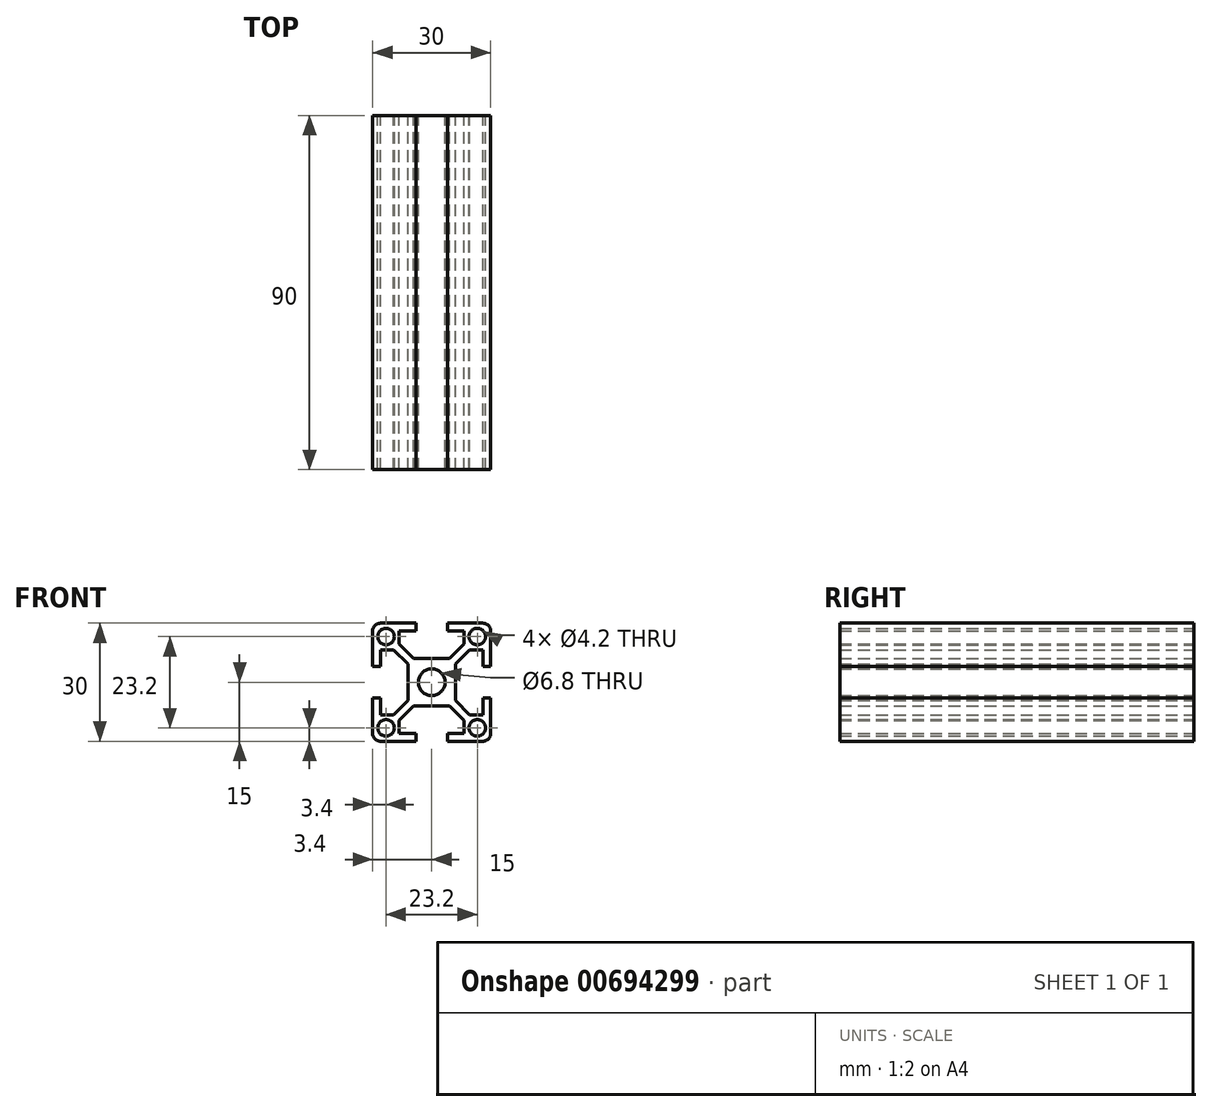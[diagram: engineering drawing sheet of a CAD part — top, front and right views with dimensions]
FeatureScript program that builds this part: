
annotation { "Feature Type Name" : "Feature", "Feature Type Description" : "" }
export const myFeature = defineFeature(function(context is Context, id is Id, definition is map)
    precondition{}
    {
        {
            var Q0;
            Q0=qCreatedBy(makeId("Front.planeOp"),FACE);
            var sketch = newSketch(context, id + "F0", { "sketchPlane" : qUnion([Q0])});
            skLineSegment(sketch, "E0", {"start": v(0, 6) * mm, "end": v(-4.59, 6) * mm});
            skLineSegment(sketch, "E1", {"start": v(-4.59, 6) * mm, "end": v(-8.25, 9.66) * mm});
            skLineSegment(sketch, "E2", {"start": v(-8.25, 9.66) * mm, "end": v(-8.25, 13) * mm});
            skLineSegment(sketch, "E3", {"start": v(-8.25, 13) * mm, "end": v(-4, 13) * mm});
            skLineSegment(sketch, "E4", {"start": v(-4, 13) * mm, "end": v(-4, 15) * mm});
            skLineSegment(sketch, "E5", {"start": v(-4, 15) * mm, "end": v(-13, 15) * mm});
            skLineSegment(sketch, "E6", {"start": v(-15, 13) * mm, "end": v(-15, 4) * mm});
            skLineSegment(sketch, "E7", {"start": v(-15, 4) * mm, "end": v(-13, 4) * mm});
            skLineSegment(sketch, "E8", {"start": v(-13, 4) * mm, "end": v(-13, 8.25) * mm});
            skLineSegment(sketch, "E9", {"start": v(-13, 8.25) * mm, "end": v(-9.66, 8.25) * mm});
            skLineSegment(sketch, "E10", {"start": v(-9.66, 8.25) * mm, "end": v(-6, 4.59) * mm});
            skLineSegment(sketch, "E11", {"start": v(-6, 4.59) * mm, "end": v(-6, 0) * mm});
            skLineSegment(sketch, "E12", {"start": v(-6, 0) * mm, "end": v(0, 0) * mm, "construction": true});
            skLineSegment(sketch, "E13", {"start": v(0, 0) * mm, "end": v(0, 6) * mm, "construction": true});
            skArc(sketch, "E14", {"start": v(0, 3.4) * mm, "mid": v(-2.4, 2.4) * mm, "end": v(-3.4, 0) * mm});
            skCircle(sketch, "E15", {"center": v(-11.6, 11.6) * mm, "radius": 2.1 * mm});
            skLineSegment(sketch, "E16", {"start": v(0, 0) * mm, "end": v(-7.38, 7.38) * mm, "construction": true});
            skLineSegment(sketch, "E17.1.0", {"start": v(-8.25, -13) * mm, "end": v(-8.25, -9.66) * mm});
            skLineSegment(sketch, "E17.1.1", {"start": v(-4, -15) * mm, "end": v(-4, -13) * mm});
            skLineSegment(sketch, "E17.1.2", {"start": v(-4, -13) * mm, "end": v(-8.25, -13) * mm});
            skLineSegment(sketch, "E17.1.3", {"start": v(-15, -4) * mm, "end": v(-15, -13) * mm});
            skLineSegment(sketch, "E17.1.4", {"start": v(-8.25, -9.66) * mm, "end": v(-4.59, -6) * mm});
            skLineSegment(sketch, "E17.1.5", {"start": v(-13, -15) * mm, "end": v(-4, -15) * mm});
            skLineSegment(sketch, "E17.1.6", {"start": v(-4.59, -6) * mm, "end": v(0, -6) * mm});
            skLineSegment(sketch, "E17.1.7", {"start": v(0, -6) * mm, "end": v(0, 0) * mm, "construction": true});
            skLineSegment(sketch, "E17.1.8", {"start": v(0, 0) * mm, "end": v(-6, 0) * mm, "construction": true});
            skLineSegment(sketch, "E17.1.9", {"start": v(-13, -4) * mm, "end": v(-15, -4) * mm});
            skLineSegment(sketch, "E17.1.10", {"start": v(-13, -8.25) * mm, "end": v(-13, -4) * mm});
            skArc(sketch, "E17.1.11", {"start": v(-3.4, 0) * mm, "mid": v(-2.4, -2.4) * mm, "end": v(0, -3.4) * mm});
            skLineSegment(sketch, "E17.1.12", {"start": v(-9.66, -8.25) * mm, "end": v(-13, -8.25) * mm});
            skLineSegment(sketch, "E17.1.13", {"start": v(0, 0) * mm, "end": v(-7.38, -7.38) * mm, "construction": true});
            skLineSegment(sketch, "E17.1.14", {"start": v(-6, -4.59) * mm, "end": v(-9.66, -8.25) * mm});
            skCircle(sketch, "E17.1.15", {"center": v(-11.6, -11.6) * mm, "radius": 2.1 * mm});
            skLineSegment(sketch, "E17.1.16", {"start": v(-6, 0) * mm, "end": v(-6, -4.59) * mm});
            skLineSegment(sketch, "E17.2.0", {"start": v(13, -8.25) * mm, "end": v(9.66, -8.25) * mm});
            skLineSegment(sketch, "E17.2.1", {"start": v(15, -4) * mm, "end": v(13, -4) * mm});
            skLineSegment(sketch, "E17.2.2", {"start": v(13, -4) * mm, "end": v(13, -8.25) * mm});
            skLineSegment(sketch, "E17.2.3", {"start": v(4, -15) * mm, "end": v(13, -15) * mm});
            skLineSegment(sketch, "E17.2.4", {"start": v(9.66, -8.25) * mm, "end": v(6, -4.59) * mm});
            skLineSegment(sketch, "E17.2.5", {"start": v(15, -13) * mm, "end": v(15, -4) * mm});
            skLineSegment(sketch, "E17.2.6", {"start": v(6, -4.59) * mm, "end": v(6, 0) * mm});
            skLineSegment(sketch, "E17.2.7", {"start": v(6, 0) * mm, "end": v(0, 0) * mm, "construction": true});
            skLineSegment(sketch, "E17.2.8", {"start": v(0, 0) * mm, "end": v(0, -6) * mm, "construction": true});
            skLineSegment(sketch, "E17.2.9", {"start": v(4, -13) * mm, "end": v(4, -15) * mm});
            skLineSegment(sketch, "E17.2.10", {"start": v(8.25, -13) * mm, "end": v(4, -13) * mm});
            skArc(sketch, "E17.2.11", {"start": v(0, -3.4) * mm, "mid": v(2.4, -2.4) * mm, "end": v(3.4, 0) * mm});
            skLineSegment(sketch, "E17.2.12", {"start": v(8.25, -9.66) * mm, "end": v(8.25, -13) * mm});
            skLineSegment(sketch, "E17.2.13", {"start": v(0, 0) * mm, "end": v(7.38, -7.38) * mm, "construction": true});
            skLineSegment(sketch, "E17.2.14", {"start": v(4.59, -6) * mm, "end": v(8.25, -9.66) * mm});
            skCircle(sketch, "E17.2.15", {"center": v(11.6, -11.6) * mm, "radius": 2.1 * mm});
            skLineSegment(sketch, "E17.2.16", {"start": v(0, -6) * mm, "end": v(4.59, -6) * mm});
            skLineSegment(sketch, "E17.3.0", {"start": v(8.25, 13) * mm, "end": v(8.25, 9.66) * mm});
            skLineSegment(sketch, "E17.3.1", {"start": v(4, 15) * mm, "end": v(4, 13) * mm});
            skLineSegment(sketch, "E17.3.2", {"start": v(4, 13) * mm, "end": v(8.25, 13) * mm});
            skLineSegment(sketch, "E17.3.3", {"start": v(15, 4) * mm, "end": v(15, 13) * mm});
            skLineSegment(sketch, "E17.3.4", {"start": v(8.25, 9.66) * mm, "end": v(4.59, 6) * mm});
            skLineSegment(sketch, "E17.3.5", {"start": v(13, 15) * mm, "end": v(4, 15) * mm});
            skLineSegment(sketch, "E17.3.6", {"start": v(4.59, 6) * mm, "end": v(0, 6) * mm});
            skLineSegment(sketch, "E17.3.7", {"start": v(0, 6) * mm, "end": v(0, 0) * mm, "construction": true});
            skLineSegment(sketch, "E17.3.8", {"start": v(0, 0) * mm, "end": v(6, 0) * mm, "construction": true});
            skLineSegment(sketch, "E17.3.9", {"start": v(13, 4) * mm, "end": v(15, 4) * mm});
            skLineSegment(sketch, "E17.3.10", {"start": v(13, 8.25) * mm, "end": v(13, 4) * mm});
            skArc(sketch, "E17.3.11", {"start": v(3.4, 0) * mm, "mid": v(2.4, 2.4) * mm, "end": v(0, 3.4) * mm});
            skLineSegment(sketch, "E17.3.12", {"start": v(9.66, 8.25) * mm, "end": v(13, 8.25) * mm});
            skLineSegment(sketch, "E17.3.13", {"start": v(0, 0) * mm, "end": v(7.38, 7.38) * mm, "construction": true});
            skLineSegment(sketch, "E17.3.14", {"start": v(6, 4.59) * mm, "end": v(9.66, 8.25) * mm});
            skCircle(sketch, "E17.3.15", {"center": v(11.6, 11.6) * mm, "radius": 2.1 * mm});
            skLineSegment(sketch, "E17.3.16", {"start": v(6, 0) * mm, "end": v(6, 4.59) * mm});
            skPoint(sketch, "E18.visualSharp", {"position": v(-15, 15) * mm});
            skArc(sketch, "E18.filletArc", {"start": v(-13, 15) * mm, "mid": v(-14.41, 14.41) * mm, "end": v(-15, 13) * mm});
            skPoint(sketch, "E19.visualSharp", {"position": v(15, 15) * mm});
            skArc(sketch, "E19.filletArc", {"start": v(15, 13) * mm, "mid": v(14.41, 14.41) * mm, "end": v(13, 15) * mm});
            skPoint(sketch, "E20.visualSharp", {"position": v(15, -15) * mm});
            skArc(sketch, "E20.filletArc", {"start": v(13, -15) * mm, "mid": v(14.41, -14.41) * mm, "end": v(15, -13) * mm});
            skPoint(sketch, "E21.visualSharp", {"position": v(-15, -15) * mm});
            skArc(sketch, "E21.filletArc", {"start": v(-15, -13) * mm, "mid": v(-14.41, -14.41) * mm, "end": v(-13, -15) * mm});
            skSolve(sketch);
        }
        {
            var Q0;
            Q0=qSketchRegion(id+"F0",true);
            extrude(context, id + "F1", {"entities" : qUnion([Q0]), "depth" : 90 * mm, "offsetDistance" : 25 * mm});
        }
    });
